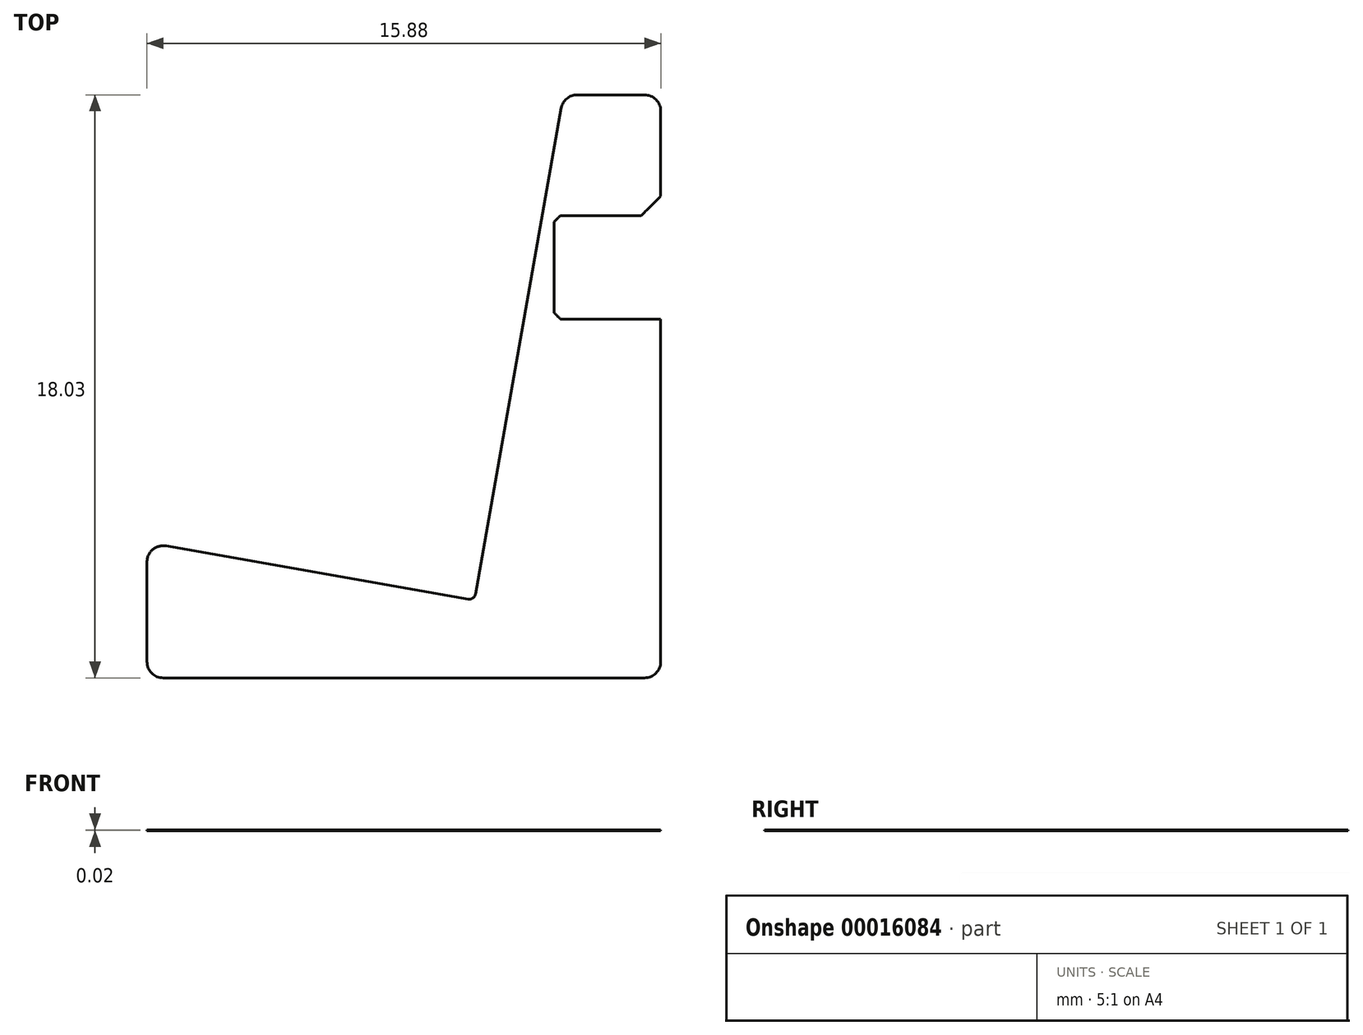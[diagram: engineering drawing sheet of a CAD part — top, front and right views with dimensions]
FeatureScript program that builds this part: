
annotation { "Feature Type Name" : "Feature", "Feature Type Description" : "" }
export const myFeature = defineFeature(function(context is Context, id is Id, definition is map)
    precondition{}
    {
        {
            var Q0;
            Q0=qCreatedBy(makeId("Top.planeOp"),FACE);
            var sketch = newSketch(context, id + "F0", { "sketchPlane" : qUnion([Q0])});
            skLineSegment(sketch, "E0", {"start": v(1.98, 2.43) * mm, "end": v(-7.35, 4.08) * mm});
            skLineSegment(sketch, "E1", {"start": v(-7.94, 3.59) * mm, "end": v(-7.94, 0) * mm});
            skLineSegment(sketch, "E2", {"start": v(-7.94, 0) * mm, "end": v(7.94, 0) * mm});
            skLineSegment(sketch, "E3", {"start": v(7.94, 0) * mm, "end": v(7.94, 17.53) * mm});
            skLineSegment(sketch, "E4", {"start": v(2.22, 2.6) * mm, "end": v(4.86, 17.62) * mm});
            skLineSegment(sketch, "E5", {"start": v(5.36, 18.03) * mm, "end": v(7.44, 18.03) * mm});
            skPoint(sketch, "E6.visualSharp", {"position": v(4.94, 18.03) * mm});
            skArc(sketch, "E6.filletArc", {"start": v(5.36, 18.03) * mm, "mid": v(5.04, 17.92) * mm, "end": v(4.86, 17.62) * mm});
            skPoint(sketch, "E7.visualSharp", {"position": v(7.94, 18.03) * mm});
            skArc(sketch, "E7.filletArc", {"start": v(7.94, 17.53) * mm, "mid": v(7.8, 17.89) * mm, "end": v(7.44, 18.03) * mm});
            skPoint(sketch, "E8.visualSharp", {"position": v(-7.94, 4.18) * mm});
            skArc(sketch, "E8.filletArc", {"start": v(-7.35, 4.08) * mm, "mid": v(-7.76, 3.97) * mm, "end": v(-7.94, 3.59) * mm});
            skPoint(sketch, "E9.visualSharp", {"position": v(2.18, 2.4) * mm});
            skArc(sketch, "E9.filletArc", {"start": v(1.98, 2.43) * mm, "mid": v(2.13, 2.47) * mm, "end": v(2.22, 2.6) * mm});
            skSolve(sketch);
        }
        {
            var Q0;
            Q0=qSketchRegion(id+"F0",true);
            var Q1;
            Q1=makeQuery(id+"F0.imprint","IMPRINT",FACE,{"disambiguationData":[TD([[makeQuery(id+"F0.imprint","IMPRINT",EDGE,{"derivedFrom":sQuery(id+"F0.wireOp",EDGE,"0de830e7-9daf-4a68-be67-74efd37edb9d.0")}),-1.0]])]});
            extrude(context, id + "F1", {"entities" : qUnion([Q0, Q1]), "endBound" : BoundingType.SYMMETRIC, "depth" : 5 / 203.2 * mm});
        }
        {
            var Q0;
            Q0=makeQuery(id+"F1.opExtrude","SWEPT_EDGE",EDGE,{"disambiguationData":[OSD([sQuery(id+"F0.wireOp",EDGE,"E4"),sQuery(id+"F0.wireOp",EDGE,"E5")])]});
            var Q1;
            Q1=makeQuery(id+"F1.opExtrude","SWEPT_EDGE",EDGE,{"disambiguationData":[OSD([sQuery(id+"F0.wireOp",EDGE,"E0"),sQuery(id+"F0.wireOp",EDGE,"E1")])]});
            var Q2;
            Q2=makeQuery(id+"F1.opExtrude","SWEPT_EDGE",EDGE,{"disambiguationData":[OSD([sQuery(id+"F0.wireOp",EDGE,"E3"),sQuery(id+"F0.wireOp",EDGE,"E5")])]});
            fillet(context, id + "F2", {"entities" : qUnion([Q0, Q1, Q2]), "radius" : .5 * mm, "tangentPropagation" : true, "allowEdgeOverflow" : false});
        }
        {
            var Q0;
            Q0=makeQuery(id+"F1.opExtrude","SWEPT_FACE",FACE,{"disambiguationData":[OSD([sQuery(id+"F0.wireOp",EDGE,"E3")])]});
            var sketch = newSketch(context, id + "F3", { "sketchPlane" : qUnion([Q0])});
            skCircle(sketch, "E10", {"center": v(4.76, 3.18) * mm, "radius": 1.6 * mm});
            skCircle(sketch, "E11", {"center": v(4.76, -3.17) * mm, "radius": 1.6 * mm});
            skCircle(sketch, "E12", {"center": v(12.7, 0) * mm, "radius": 1.6 * mm});
            skSolve(sketch);
        }
        {
            var Q0;
            Q0=qSketchRegion(id+"F3",true);
            extrude(context, id + "F4", {"entities" : qUnion([Q0]), "operationType" : NewBodyOperationType.REMOVE, "oppositeDirection" : true, "depth" : 3.3 * mm});
        }
        {
            var Q0;
            Q0=makeQuery(id+"F4.boolean.opBoolean","COPY",EDGE,{"derivedFrom":makeQuery(id+"F4.opExtrude","CAP_EDGE",EDGE,{"disambiguationData":[OSD([sQuery(id+"F3.wireOp",EDGE,"E12")])],"isStart":false})});
            var Q1;
            Q1=makeQuery(id+"F4.boolean.opBoolean","COPY",EDGE,{"derivedFrom":makeQuery(id+"F4.opExtrude","CAP_EDGE",EDGE,{"disambiguationData":[OSD([sQuery(id+"F3.wireOp",EDGE,"E10")])],"isStart":false})});
            var Q2;
            Q2=makeQuery(id+"F4.boolean.opBoolean","COPY",EDGE,{"derivedFrom":makeQuery(id+"F4.opExtrude","CAP_EDGE",EDGE,{"disambiguationData":[OSD([sQuery(id+"F3.wireOp",EDGE,"E11")])],"isStart":false})});
            chamfer(context, id + "F5", {"entities" : qUnion([Q0, Q1, Q2]), "width" : .2 * mm, "tangentPropagation" : true});
        }
        {
            var Q0;
            Q0=makeQuery(id+"F4.boolean.opBoolean","COPY",EDGE,{"derivedFrom":makeQuery(id+"F4.opExtrude","CAP_EDGE",EDGE,{"disambiguationData":[OSD([sQuery(id+"F3.wireOp",EDGE,"E12")])],"isStart":true})});
            var Q1;
            Q1=makeQuery(id+"F4.boolean.opBoolean","COPY",EDGE,{"derivedFrom":makeQuery(id+"F4.opExtrude","CAP_EDGE",EDGE,{"disambiguationData":[OSD([sQuery(id+"F3.wireOp",EDGE,"E10")])],"isStart":true})});
            var Q2;
            Q2=makeQuery(id+"F4.boolean.opBoolean","COPY",EDGE,{"derivedFrom":makeQuery(id+"F4.opExtrude","CAP_EDGE",EDGE,{"disambiguationData":[OSD([sQuery(id+"F3.wireOp",EDGE,"E11")])],"isStart":true})});
            chamfer(context, id + "F6", {"entities" : qUnion([Q0, Q1, Q2]), "width" : .6 * mm, "tangentPropagation" : true});
        }
    });
